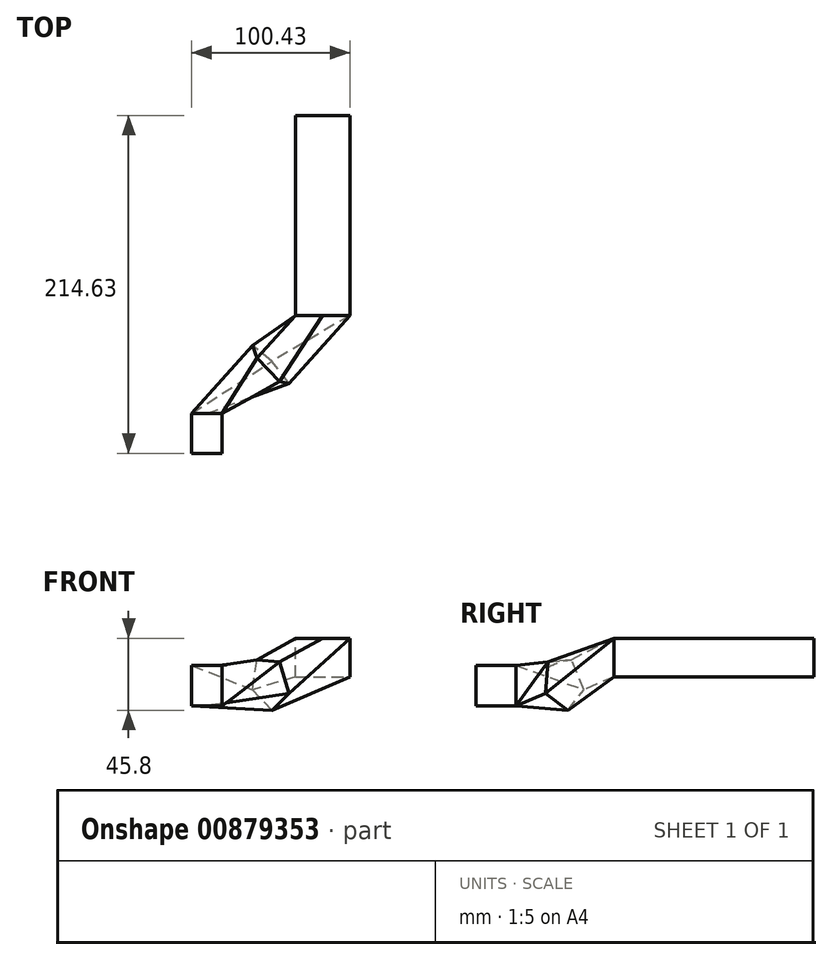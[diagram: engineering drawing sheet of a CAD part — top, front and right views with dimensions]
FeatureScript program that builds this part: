
annotation { "Feature Type Name" : "Feature", "Feature Type Description" : "" }
export const myFeature = defineFeature(function(context is Context, id is Id, definition is map)
    precondition{}
    {
        {
            var Q0;
            Q0=qCreatedBy(makeId("Front.planeOp"),FACE);
            var sketch = newSketch(context, id + "F0", { "sketchPlane" : qUnion([Q0])});
            skLineSegment(sketch, "E0.bottom", {"start": v(0, 0) * mm, "end": v(34.54, 0) * mm});
            skLineSegment(sketch, "E0.top", {"start": v(0, 24.6) * mm, "end": v(34.54, 24.6) * mm});
            skLineSegment(sketch, "E0.left", {"start": v(0, 0) * mm, "end": v(0, 24.6) * mm});
            skLineSegment(sketch, "E0.right", {"start": v(34.54, 0) * mm, "end": v(34.54, 24.6) * mm});
            skSolve(sketch);
        }
        {
            var Q0;
            Q0 = qSketchRegion(id + "F0", true);
            extrude(context, id + "F1", {"entities" : qUnion([Q0]), "depth" : 127 * mm, "offsetDistance" : 25.4 * mm});
        }
        {
            var Q0;
            Q0=makeQuery(id+"F1.opExtrude","CAP_FACE",FACE,{"disambiguationData":[OSD([sQuery(id+"F0.wireOp",EDGE,"E0.bottom"),sQuery(id+"F0.wireOp",EDGE,"E0.top"),sQuery(id+"F0.wireOp",EDGE,"E0.left"),sQuery(id+"F0.wireOp",EDGE,"E0.right")])],"isStart":false});
            cPlane(context, id + "F2", {"entities" : qUnion([Q0]), "cplaneType" : CPlaneType.OFFSET, "offset" : 62.23 * mm, "width" : 152.4 * mm, "height" : 152.4 * mm});
        }
        {
            var Q0;
            Q0=qCreatedBy(id+"F2.planeOp",FACE);
            var sketch = newSketch(context, id + "F3", { "sketchPlane" : qUnion([Q0])});
            skLineSegment(sketch, "E1", {"start": v(15.6, 10.8) * mm, "end": v(-46.56, 7.41) * mm});
            skLineSegment(sketch, "E2.bottom", {"start": v(-46.56, 7.41) * mm, "end": v(-65.89, 7.41) * mm});
            skLineSegment(sketch, "E2.top", {"start": v(-46.56, -18.32) * mm, "end": v(-65.89, -18.32) * mm});
            skLineSegment(sketch, "E2.left", {"start": v(-46.56, 7.41) * mm, "end": v(-46.56, -18.32) * mm});
            skLineSegment(sketch, "E2.right", {"start": v(-65.89, 7.41) * mm, "end": v(-65.89, -18.32) * mm});
            skSolve(sketch);
        }
        {
            var Q0;
            Q0=makeQuery(id+"F1.opExtrude","CAP_VERTEX",VERTEX,{"disambiguationData":[OSD([sQuery(id+"F0.wireOp",EDGE,"E0.top"),sQuery(id+"F0.wireOp",EDGE,"E0.left")])],"isStart":false});
            var Q1;
            Q1=makeQuery(id+"F1.opExtrude","CAP_VERTEX",VERTEX,{"disambiguationData":[OSD([sQuery(id+"F0.wireOp",EDGE,"E0.bottom"),sQuery(id+"F0.wireOp",EDGE,"E0.left")])],"isStart":false});
            var Q2;
            Q2=sQuery(id+"F3.wireOp",VERTEX,"E2.bottom.end");
            cPlane(context, id + "F4", {"entities" : qUnion([Q0, Q1, Q2]), "cplaneType" : CPlaneType.THREE_POINT, "offset" : 25.4 * mm, "width" : 152.4 * mm, "height" : 152.4 * mm});
        }
        {
            var Q0;
            Q0=qCreatedBy(id+"F2.planeOp",FACE);
            var sketch = newSketch(context, id + "F5", { "sketchPlane" : qUnion([Q0])});
            skSolve(sketch);
        }
        {
            var Q0;
            Q0 = qSketchRegion(id + "F5", true);
            var Q1;
            Q1=makeQuery(id+"F3.imprint","IMPRINT",FACE,{"disambiguationData":[TD([[makeQuery(id+"F3.imprint","IMPRINT",EDGE,{"derivedFrom":sQuery(id+"F3.wireOp",EDGE,"E2.bottom")}),1.0]])]});
            extrude(context, id + "F6", {"entities" : qUnion([Q0, Q1]), "depth" : 25.4 * mm, "offsetDistance" : 25.4 * mm});
        }
        {
            var Q0;
            Q0=qCreatedBy(id+"F4.planeOp",FACE);
            cPlane(context, id + "F7", {"entities" : qUnion([Q0]), "cplaneType" : CPlaneType.OFFSET, "offset" : 10.16 * mm, "width" : 152.4 * mm, "height" : 152.4 * mm});
        }
        {
            var Q0;
            Q0=qCreatedBy(id+"F7.planeOp",FACE);
            var sketch = newSketch(context, id + "F8", { "sketchPlane" : qUnion([Q0])});
            skLineSegment(sketch, "E3", {"start": v(-77.6, 12.07) * mm, "end": v(-167.05, -3.05) * mm});
            skSolve(sketch);
        }
        {
            var Q0;
            Q0=sQuery(id+"F8.wireOp",EDGE,"E3");
            cPoint(context, id + "F9", {"entities" : qUnion([Q0]), "parameter" : 0.5});
        }
        {
            var Q0;
            Q0 = qCreatedBy(id + "F9" ,VERTEX);
            var Q1;
            Q1=sQuery(id+"F8.wireOp",EDGE,"E3");
            cPlane(context, id + "F10", {"entities" : qUnion([Q0, Q1]), "cplaneType" : CPlaneType.LINE_POINT, "offset" : 25.4 * mm, "width" : 152.4 * mm, "height" : 152.4 * mm});
        }
        {
            var Q0;
            Q0=qCreatedBy(id+"F10.planeOp",FACE);
            var sketch = newSketch(context, id + "F11", { "sketchPlane" : qUnion([Q0])});
            skCircle(sketch, "E4.cCircle", {"center": v(105.85, 0) * mm, "radius": 14.34 * mm, "construction": true});
            skLineSegment(sketch, "E4.0", {"start": v(121.08, -9.08) * mm, "end": v(101.92, -17.29) * mm});
            skLineSegment(sketch, "E4.1", {"start": v(101.92, -17.29) * mm, "end": v(88.2, -1.6) * mm});
            skLineSegment(sketch, "E4.2", {"start": v(88.2, -1.6) * mm, "end": v(98.87, 16.3) * mm});
            skLineSegment(sketch, "E4.3", {"start": v(98.87, 16.3) * mm, "end": v(119.19, 11.68) * mm});
            skLineSegment(sketch, "E4.4", {"start": v(119.19, 11.68) * mm, "end": v(121.08, -9.08) * mm});
            skPoint(sketch, "E4.0.midPoint", {"position": v(111.5, -13.18) * mm});
            skSolve(sketch);
        }
        {
            var Q1;
            Q1=makeQuery(id+"F1.opExtrude","CAP_FACE",FACE,{"disambiguationData":[OSD([sQuery(id+"F0.wireOp",EDGE,"E0.bottom"),sQuery(id+"F0.wireOp",EDGE,"E0.top"),sQuery(id+"F0.wireOp",EDGE,"E0.left"),sQuery(id+"F0.wireOp",EDGE,"E0.right")])],"isStart":false});
            var Q2;
            Q2=makeQuery(id+"F11.imprint","IMPRINT",FACE,{"disambiguationData":[TD([[makeQuery(id+"F11.imprint","IMPRINT",EDGE,{"derivedFrom":sQuery(id+"F11.wireOp",EDGE,"E4.0")}),-1.0]])]});
            loft(context, id + "F12", {"operationType" : NewBodyOperationType.ADD, "sheetProfilesArray" : [{ "sheetProfileEntities" : qUnion([Q1]) }, { "sheetProfileEntities" : qUnion([Q2]) }]});
        }
        {
            var Q0;
            Q0=makeQuery(id+"F3.imprint","IMPRINT",FACE,{"disambiguationData":[TD([[makeQuery(id+"F3.imprint","IMPRINT",EDGE,{"derivedFrom":sQuery(id+"F3.wireOp",EDGE,"E2.bottom")}),1.0]])]});
            var Q1;
            Q1=makeQuery(id+"F12.opLoft","CAP_FACE",FACE,{"disambiguationData":[OSD([makeQuery(id+"F11.imprint","IMPRINT",FACE,{"disambiguationData":[TD([[makeQuery(id+"F11.imprint","IMPRINT",EDGE,{"derivedFrom":sQuery(id+"F11.wireOp",EDGE,"E4.0")}),-1.0]])]})])],"isStart":true});
            loft(context, id + "F13", {"sheetProfilesArray" : [{ "sheetProfileEntities" : qUnion([Q0]) }, { "sheetProfileEntities" : qUnion([Q1]) }]});
        }
    });
